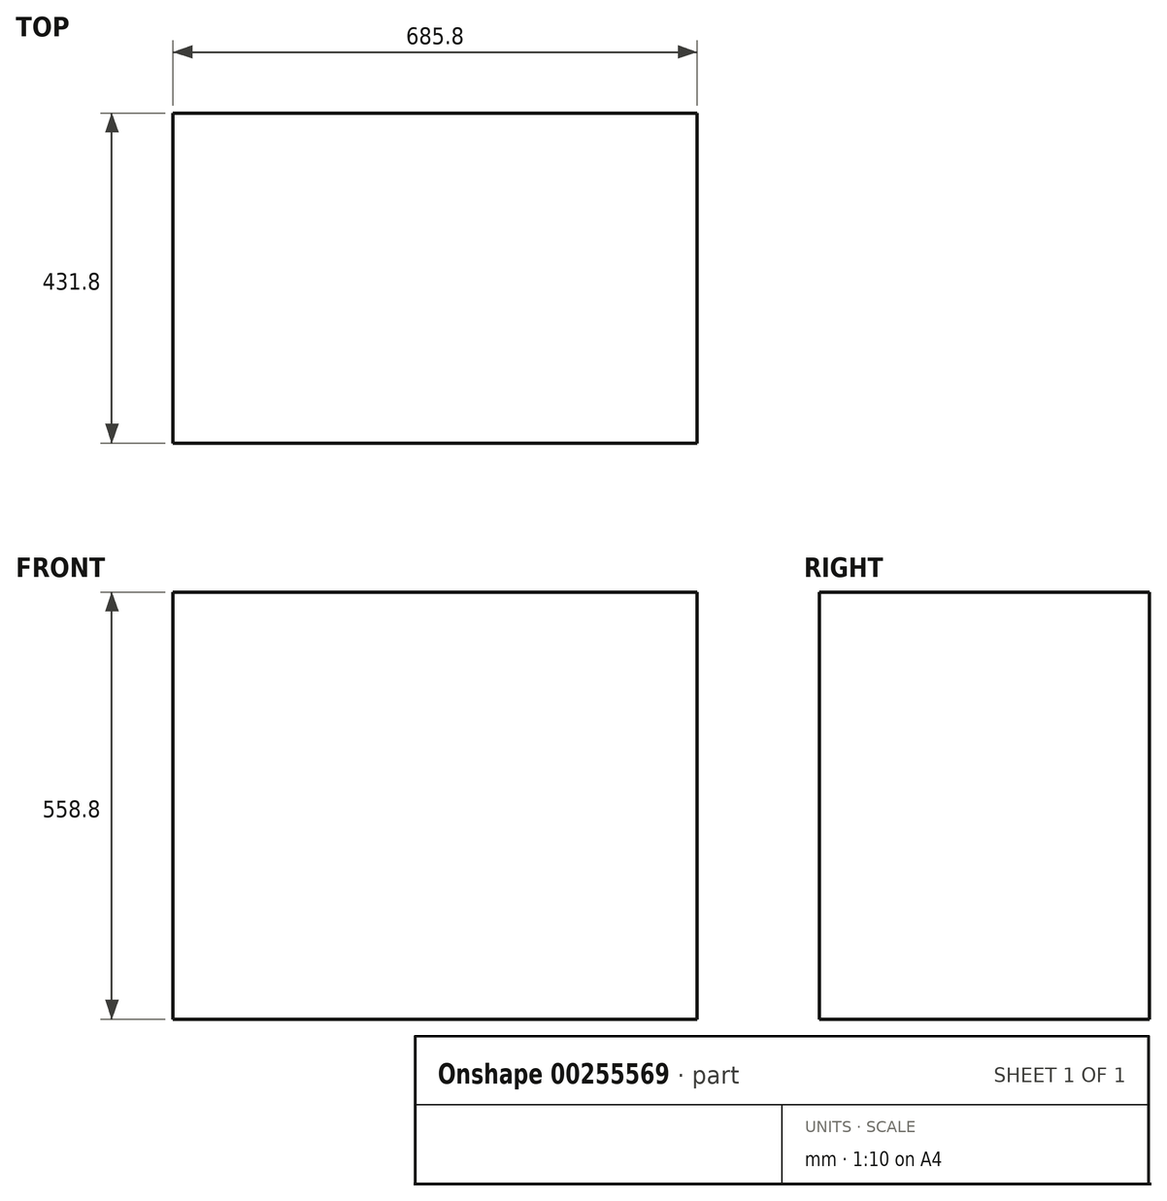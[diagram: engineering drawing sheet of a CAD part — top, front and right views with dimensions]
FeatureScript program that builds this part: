
annotation { "Feature Type Name" : "Feature", "Feature Type Description" : "" }
export const myFeature = defineFeature(function(context is Context, id is Id, definition is map)
    precondition{}
    {
        {
            var Q0;
            Q0=qCreatedBy(makeId("Front.planeOp"),FACE);
            var sketch = newSketch(context, id + "F0", { "sketchPlane" : qUnion([Q0])});
            skLineSegment(sketch, "E0.bottom", {"start": v(0, 0) * mm, "end": v(685.8, 0) * mm});
            skLineSegment(sketch, "E0.top", {"start": v(0, 558.8) * mm, "end": v(685.8, 558.8) * mm});
            skLineSegment(sketch, "E0.left", {"start": v(0, 0) * mm, "end": v(0, 558.8) * mm});
            skLineSegment(sketch, "E0.right", {"start": v(685.8, 0) * mm, "end": v(685.8, 558.8) * mm});
            skSolve(sketch);
        }
        {
            var Q0;
            Q0 = qSketchRegion(id + "F0", true);
            extrude(context, id + "F1", {"entities" : qUnion([Q0]), "depth" : 431.8 * mm});
        }
    });
